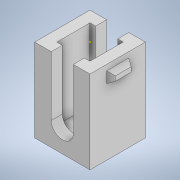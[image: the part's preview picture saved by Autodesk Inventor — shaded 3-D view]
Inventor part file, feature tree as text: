
AUTODESK INVENTOR PART (.ipt)
format: ipt  version: 2022 (Build 260153000, 153)  size: 138,240 bytes
history: native  units: in
note: dims shown in document units (in); Inventor stores cm internally (conversion verified against a paired STEP export)
features: sketch x9, extrude x4, shell x1
ambient origin geometry x8: Origin, YZ Plane, XZ Plane, XY Plane, X Axis, Y Axis, Z Axis, Center Point
bodies: Solid1 (feature_tree)
feature tree (14):
  extrude  "Extrusion1"  Depth=0.1969in
  shell  "Shell1"  Thickness=0.2953in
  extrude  "Extrusion3"  TaperAngle=0.0deg  [1 undecoded]
  sketch  "Sketch4"  dims[d10=0.0394in d11=0.0197in d12=-0.2061in]
  sketch  "Sketch5"  dims[d13=0.0394in d14=0.0787in]
  sketch  "Sketch6"  dims[d15=0.0394in]
  sketch  "Sketch7"  dims[d16=0.0787in]
  sketch  "Sketch8"  dims[d17=0.0394in]
  extrude  "Extrusion4"  Depth=0.0197in
  extrude  "Extrusion5"  Depth=0.0394in
  sketch  "Sketch1"  dims[d0=0.1969in d1=0.1969in d2=0.2953in d3=0.0in]
  sketch  "Sketch3"  dims[d4=0.0394in d8=0.0in d9=0.0in]
  sketch  "Sketch9"  dims[d18=0.0197in d19=-0.2061in]
  sketch  "Sketch10"
note: 1 required parameter value undecoded (feature->parameter linkage not recoverable at this tier; creation-order binding heuristic only, values carry confidence <= 0.55)
